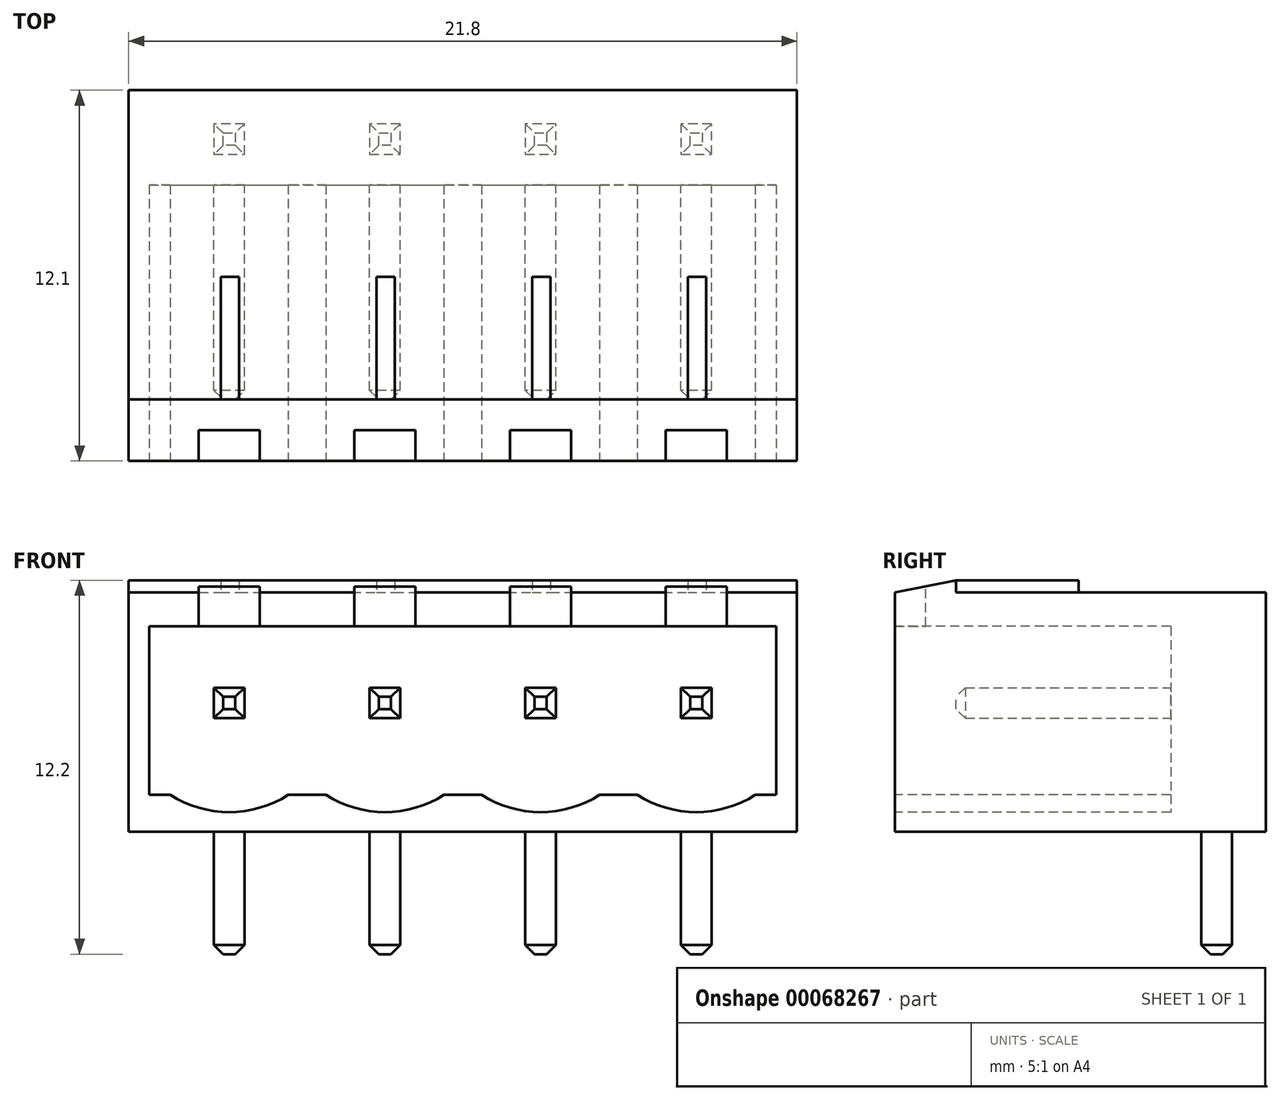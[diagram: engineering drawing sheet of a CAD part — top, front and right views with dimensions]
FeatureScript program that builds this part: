
annotation { "Feature Type Name" : "Feature", "Feature Type Description" : "" }
export const myFeature = defineFeature(function(context is Context, id is Id, definition is map)
    precondition{}
    {
        {
            var Q0;
            Q0=qCreatedBy(makeId("Front.planeOp"),FACE);
            var sketch = newSketch(context, id + "F0", { "sketchPlane" : qUnion([Q0])});
            skLineSegment(sketch, "E0.bottom", {"start": v(-10.9, 4.1) * mm, "end": v(10.9, 4.1) * mm});
            skLineSegment(sketch, "E0.top", {"start": v(-10.9, -4.1) * mm, "end": v(10.9, -4.1) * mm});
            skLineSegment(sketch, "E0.left", {"start": v(-10.9, 4.1) * mm, "end": v(-10.9, -4.1) * mm});
            skLineSegment(sketch, "E0.right", {"start": v(10.9, 4.1) * mm, "end": v(10.9, -4.1) * mm});
            skPoint(sketch, "E0.middle", {"position": v(0, 0) * mm});
            skSolve(sketch);
        }
        {
            var Q0;
            Q0=makeQuery(id+"F0.imprint","IMPRINT",FACE,{"disambiguationData":[TD([[makeQuery(id+"F0.imprint","IMPRINT",EDGE,{"derivedFrom":sQuery(id+"F0.wireOp",EDGE,"E0.bottom")}),-1.0]])]});
            extrude(context, id + "F1", {"entities" : qUnion([Q0]), "endBound" : BoundingType.SYMMETRIC, "depth" : 12.1 * mm});
        }
        {
            var Q0;
            Q0=makeQuery(id+"F1.opExtrude","CAP_FACE",FACE,{"disambiguationData":[OSD([sQuery(id+"F0.wireOp",EDGE,"E0.bottom"),sQuery(id+"F0.wireOp",EDGE,"E0.top"),sQuery(id+"F0.wireOp",EDGE,"E0.left"),sQuery(id+"F0.wireOp",EDGE,"E0.right")])],"isStart":false});
            var sketch = newSketch(context, id + "F2", { "sketchPlane" : qUnion([Q0])});
            skPoint(sketch, "E1.middle", {"position": v(0, 0) * mm});
            skLineSegment(sketch, "E2.bottom", {"start": v(-10.23, 2.6) * mm, "end": v(10.23, 2.6) * mm});
            skLineSegment(sketch, "E2.top", {"start": v(-10.23, -2.4) * mm, "end": v(10.23, -2.4) * mm, "construction": true});
            skLineSegment(sketch, "E2.left", {"start": v(-10.23, 2.6) * mm, "end": v(-10.23, -2.4) * mm});
            skLineSegment(sketch, "E2.right", {"start": v(10.23, 2.6) * mm, "end": v(10.23, -2.4) * mm});
            skPoint(sketch, "E3", {"position": v(-2.54, 0.1) * mm});
            skPoint(sketch, "E4", {"position": v(-7.62, 0.1) * mm});
            skLineSegment(sketch, "E5", {"start": v(-10.23, 0.1) * mm, "end": v(10.23, 0.1) * mm, "construction": true});
            skArc(sketch, "E6", {"start": v(0, -2.4) * mm, "mid": v(-2.54, -3.46) * mm, "end": v(-5.08, -2.4) * mm});
            skArc(sketch, "E7", {"start": v(-5.08, -2.4) * mm, "mid": v(-7.62, -3.46) * mm, "end": v(-10.16, -2.4) * mm});
            skLineSegment(sketch, "E8", {"start": v(0, 12.68) * mm, "end": v(0, -9.6) * mm, "construction": true});
            skPoint(sketch, "E9", {"position": v(2.54, 0.1) * mm});
            skPoint(sketch, "E10", {"position": v(7.62, 0.1) * mm});
            skPoint(sketch, "E11", {"position": v(0, 9.54) * mm});
            skArc(sketch, "E12", {"start": v(0, -2.4) * mm, "mid": v(2.54, -3.46) * mm, "end": v(5.08, -2.4) * mm});
            skArc(sketch, "E13", {"start": v(5.08, -2.4) * mm, "mid": v(7.62, -3.46) * mm, "end": v(10.16, -2.4) * mm});
            skLineSegment(sketch, "E14", {"start": v(10.23, -2.4) * mm, "end": v(10.16, -2.4) * mm});
            skLineSegment(sketch, "E15", {"start": v(-10.16, -2.4) * mm, "end": v(-10.23, -2.4) * mm});
            skSolve(sketch);
        }
        {
            var Q0;
            Q0=qSketchRegion(id+"F2",true);
            extrude(context, id + "F3", {"entities" : qUnion([Q0]), "operationType" : NewBodyOperationType.REMOVE, "oppositeDirection" : true, "depth" : 9 * mm});
        }
        {
            var Q0;
            Q0=makeQuery(id+"F3.boolean.opBoolean","COPY",FACE,{"derivedFrom":makeQuery(id+"F3.opExtrude","CAP_FACE",FACE,{"disambiguationData":[OSD([sQuery(id+"F2.wireOp",EDGE,"E2.bottom"),sQuery(id+"F2.wireOp",EDGE,"E2.left"),sQuery(id+"F2.wireOp",EDGE,"E2.right"),sQuery(id+"F2.wireOp",EDGE,"E6"),sQuery(id+"F2.wireOp",EDGE,"E7"),sQuery(id+"F2.wireOp",EDGE,"E12"),sQuery(id+"F2.wireOp",EDGE,"E13"),sQuery(id+"F2.wireOp",EDGE,"E14"),sQuery(id+"F2.wireOp",EDGE,"E15")])],"isStart":false})});
            var sketch = newSketch(context, id + "F4", { "sketchPlane" : qUnion([Q0])});
            skLineSegment(sketch, "E16.bottom", {"start": v(-7.12, -0.4) * mm, "end": v(-8.12, -0.4) * mm});
            skLineSegment(sketch, "E16.top", {"start": v(-7.12, 0.6) * mm, "end": v(-8.12, 0.6) * mm});
            skLineSegment(sketch, "E16.left", {"start": v(-7.12, -0.4) * mm, "end": v(-7.12, 0.6) * mm});
            skLineSegment(sketch, "E16.right", {"start": v(-8.12, -0.4) * mm, "end": v(-8.12, 0.6) * mm});
            skPoint(sketch, "E16.middle", {"position": v(-7.62, 0.1) * mm});
            skLineSegment(sketch, "E17.bottom", {"start": v(-2.04, -0.4) * mm, "end": v(-3.04, -0.4) * mm});
            skLineSegment(sketch, "E17.top", {"start": v(-2.04, 0.6) * mm, "end": v(-3.04, 0.6) * mm});
            skLineSegment(sketch, "E17.left", {"start": v(-2.04, -0.4) * mm, "end": v(-2.04, 0.6) * mm});
            skLineSegment(sketch, "E17.right", {"start": v(-3.04, -0.4) * mm, "end": v(-3.04, 0.6) * mm});
            skPoint(sketch, "E17.middle", {"position": v(-2.54, 0.1) * mm});
            skLineSegment(sketch, "E18.bottom", {"start": v(3.04, -0.4) * mm, "end": v(2.04, -0.4) * mm});
            skLineSegment(sketch, "E18.top", {"start": v(3.04, 0.6) * mm, "end": v(2.04, 0.6) * mm});
            skLineSegment(sketch, "E18.left", {"start": v(3.04, -0.4) * mm, "end": v(3.04, 0.6) * mm});
            skLineSegment(sketch, "E18.right", {"start": v(2.04, -0.4) * mm, "end": v(2.04, 0.6) * mm});
            skPoint(sketch, "E18.middle", {"position": v(2.54, 0.1) * mm});
            skLineSegment(sketch, "E19.bottom", {"start": v(8.12, -0.4) * mm, "end": v(7.12, -0.4) * mm});
            skLineSegment(sketch, "E19.top", {"start": v(8.12, 0.6) * mm, "end": v(7.12, 0.6) * mm});
            skLineSegment(sketch, "E19.left", {"start": v(8.12, -0.4) * mm, "end": v(8.12, 0.6) * mm});
            skLineSegment(sketch, "E19.right", {"start": v(7.12, -0.4) * mm, "end": v(7.12, 0.6) * mm});
            skPoint(sketch, "E19.middle", {"position": v(7.62, 0.1) * mm});
            skLineSegment(sketch, "E20", {"start": v(10.9, 0.1) * mm, "end": v(-10.9, 0.1) * mm, "construction": true});
            skPoint(sketch, "E20.startSnap0", {"position": v(10.23, 0.1) * mm});
            skPoint(sketch, "E20.endSnap0", {"position": v(-10.23, 0.1) * mm});
            skLineSegment(sketch, "E21", {"start": v(0, 4.1) * mm, "end": v(0, -4.1) * mm, "construction": true});
            skPoint(sketch, "E21.startSnap0", {"position": v(0, 2.6) * mm});
            skSolve(sketch);
        }
        {
            var Q0;
            Q0=qSketchRegion(id+"F4",true);
            var Q1;
            Q1=makeQuery(id+"F1.opExtrude","CAP_FACE",FACE,{"disambiguationData":[OSD([sQuery(id+"F0.wireOp",EDGE,"E0.bottom"),sQuery(id+"F0.wireOp",EDGE,"E0.top"),sQuery(id+"F0.wireOp",EDGE,"E0.left"),sQuery(id+"F0.wireOp",EDGE,"E0.right")])],"isStart":false});
            extrude(context, id + "F5", {"entities" : qUnion([Q0]), "endBoundEntityFace" : qUnion([Q1]), "depth" : 7 * mm});
        }
        {
            var Q0;
            Q0=makeQuery(id+"F1.opExtrude","SWEPT_FACE",FACE,{"disambiguationData":[OSD([sQuery(id+"F0.wireOp",EDGE,"E0.top")])]});
            var sketch = newSketch(context, id + "F6", { "sketchPlane" : qUnion([Q0])});
            skLineSegment(sketch, "E22", {"start": v(0, 6.05) * mm, "end": v(0, -6.05) * mm, "construction": true});
            skLineSegment(sketch, "E23.bottom", {"start": v(-8.12, -3.95) * mm, "end": v(-7.12, -3.95) * mm});
            skLineSegment(sketch, "E23.top", {"start": v(-8.12, -4.95) * mm, "end": v(-7.12, -4.95) * mm});
            skLineSegment(sketch, "E23.left", {"start": v(-8.12, -3.95) * mm, "end": v(-8.12, -4.95) * mm});
            skLineSegment(sketch, "E23.right", {"start": v(-7.12, -3.95) * mm, "end": v(-7.12, -4.95) * mm});
            skPoint(sketch, "E23.middle", {"position": v(-7.62, -4.45) * mm});
            skLineSegment(sketch, "E24.bottom", {"start": v(-3.04, -3.95) * mm, "end": v(-2.04, -3.95) * mm});
            skLineSegment(sketch, "E24.top", {"start": v(-3.04, -4.95) * mm, "end": v(-2.04, -4.95) * mm});
            skLineSegment(sketch, "E24.left", {"start": v(-3.04, -3.95) * mm, "end": v(-3.04, -4.95) * mm});
            skLineSegment(sketch, "E24.right", {"start": v(-2.04, -3.95) * mm, "end": v(-2.04, -4.95) * mm});
            skPoint(sketch, "E24.middle", {"position": v(-2.54, -4.45) * mm});
            skLineSegment(sketch, "E25", {"start": v(-10.9, -4.45) * mm, "end": v(10.9, -4.45) * mm, "construction": true});
            skPoint(sketch, "E25.startSnap0", {"position": v(-8.12, -4.45) * mm});
            skLineSegment(sketch, "E26.MirrorCS", {"start": v(8.12, -3.95) * mm, "end": v(8.12, -4.95) * mm});
            skLineSegment(sketch, "E27.MirrorCS", {"start": v(7.12, -3.95) * mm, "end": v(7.12, -4.95) * mm});
            skLineSegment(sketch, "E28.MirrorCS", {"start": v(3.04, -3.95) * mm, "end": v(2.04, -3.95) * mm});
            skLineSegment(sketch, "E29.MirrorCS", {"start": v(3.04, -4.95) * mm, "end": v(2.04, -4.95) * mm});
            skLineSegment(sketch, "E30.MirrorCS", {"start": v(8.12, -4.95) * mm, "end": v(7.12, -4.95) * mm});
            skPoint(sketch, "E31.MirrorP", {"position": v(2.54, -4.45) * mm});
            skLineSegment(sketch, "E32.MirrorCS", {"start": v(3.04, -3.95) * mm, "end": v(3.04, -4.95) * mm});
            skLineSegment(sketch, "E33.MirrorCS", {"start": v(2.04, -3.95) * mm, "end": v(2.04, -4.95) * mm});
            skPoint(sketch, "E34.MirrorP", {"position": v(8.12, -4.45) * mm});
            skPoint(sketch, "E35.MirrorP", {"position": v(7.62, -4.45) * mm});
            skLineSegment(sketch, "E36.MirrorCS", {"start": v(8.12, -3.95) * mm, "end": v(7.12, -3.95) * mm});
            skSolve(sketch);
        }
        {
            var Q0;
            Q0=qSketchRegion(id+"F6",true);
            extrude(context, id + "F7", {"entities" : qUnion([Q0]), "depth" : 4 * mm});
        }
        {
            var Q0;
            Q0=makeQuery(id+"F1.opExtrude","SWEPT_FACE",FACE,{"disambiguationData":[OSD([sQuery(id+"F0.wireOp",EDGE,"E0.bottom")])]});
            var sketch = newSketch(context, id + "F8", { "sketchPlane" : qUnion([Q0])});
            skLineSegment(sketch, "E37", {"start": v(0, 6.05) * mm, "end": v(0, -6.05) * mm, "construction": true});
            skLineSegment(sketch, "E38.bottom", {"start": v(-3.54, -5.05) * mm, "end": v(-1.54, -5.05) * mm});
            skLineSegment(sketch, "E38.top", {"start": v(-3.54, -6.05) * mm, "end": v(-1.54, -6.05) * mm});
            skLineSegment(sketch, "E38.left", {"start": v(-3.54, -5.05) * mm, "end": v(-3.54, -6.05) * mm});
            skLineSegment(sketch, "E38.right", {"start": v(-1.54, -5.05) * mm, "end": v(-1.54, -6.05) * mm});
            skPoint(sketch, "E38.middle", {"position": v(-2.54, -5.55) * mm});
            skLineSegment(sketch, "E39.1.0.0", {"start": v(3.54, -5.05) * mm, "end": v(3.54, -6.05) * mm});
            skLineSegment(sketch, "E39.1.0.1", {"start": v(1.54, -5.05) * mm, "end": v(1.54, -6.05) * mm});
            skLineSegment(sketch, "E39.1.0.2", {"start": v(1.54, -6.05) * mm, "end": v(3.54, -6.05) * mm});
            skLineSegment(sketch, "E39.1.0.3", {"start": v(1.54, -5.05) * mm, "end": v(3.54, -5.05) * mm});
            skPoint(sketch, "E39.1.0.4", {"position": v(2.54, -5.55) * mm});
            skLineSegment(sketch, "E39.2.0.0", {"start": v(8.62, -5.05) * mm, "end": v(8.62, -6.05) * mm});
            skLineSegment(sketch, "E39.2.0.1", {"start": v(6.62, -5.05) * mm, "end": v(6.62, -6.05) * mm});
            skLineSegment(sketch, "E39.2.0.2", {"start": v(6.62, -6.05) * mm, "end": v(8.62, -6.05) * mm});
            skLineSegment(sketch, "E39.2.0.3", {"start": v(6.62, -5.05) * mm, "end": v(8.62, -5.05) * mm});
            skPoint(sketch, "E39.2.0.4", {"position": v(7.62, -5.55) * mm});
            skLineSegment(sketch, "E39.direction1", {"start": v(-1.54, -6.05) * mm, "end": v(3.54, -6.05) * mm, "construction": true});
            skLineSegment(sketch, "E40.1.0.0", {"start": v(-8.62, -5.05) * mm, "end": v(-6.62, -5.05) * mm});
            skLineSegment(sketch, "E40.1.0.1", {"start": v(-8.62, -6.05) * mm, "end": v(-6.62, -6.05) * mm});
            skLineSegment(sketch, "E40.1.0.2", {"start": v(-8.62, -5.05) * mm, "end": v(-8.62, -6.05) * mm});
            skLineSegment(sketch, "E40.1.0.3", {"start": v(-6.62, -5.05) * mm, "end": v(-6.62, -6.05) * mm});
            skPoint(sketch, "E40.1.0.4", {"position": v(-7.62, -5.55) * mm});
            skLineSegment(sketch, "E40.direction1", {"start": v(-3.54, -5.05) * mm, "end": v(-8.62, -5.05) * mm, "construction": true});
            skSolve(sketch);
        }
        {
            var Q0;
            Q0=qSketchRegion(id+"F8",true);
            extrude(context, id + "F9", {"entities" : qUnion([Q0]), "operationType" : NewBodyOperationType.REMOVE, "oppositeDirection" : true, "depth" : 2 * mm});
        }
        {
            var Q0;
            {var subQ0=sQuery(id+"F0.wireOp",EDGE,"E0.top");var subQ1=sQuery(id+"F0.wireOp",EDGE,"E0.bottom");var subQ2=sQuery(id+"F0.wireOp",EDGE,"E0.left");var subQ3=sQuery(id+"F0.wireOp",EDGE,"E0.right");Q0=makeQuery(id+"F9.boolean.opBoolean","SPLIT",FACE,{"disambiguationData":[TD([makeQuery(id+"F1.opExtrude","SWEPT_FACE",FACE,{"disambiguationData":[OSD([subQ0])]})])],"derivedFrom":makeQuery(id+"F1.opExtrude","CAP_FACE",FACE,{"disambiguationData":[OSD([subQ1,subQ0,subQ2,subQ3])],"isStart":false})});}
            var sketch = newSketch(context, id + "F10", { "sketchPlane" : qUnion([Q0])});
            skLineSegment(sketch, "E41.bottom", {"start": v(-10.23, -2.4) * mm, "end": v(10.23, -2.4) * mm});
            skLineSegment(sketch, "E41.top", {"start": v(-10.23, -2.9) * mm, "end": v(10.23, -2.9) * mm});
            skLineSegment(sketch, "E41.left", {"start": v(-10.23, -2.4) * mm, "end": v(-10.23, -2.9) * mm});
            skLineSegment(sketch, "E41.right", {"start": v(10.23, -2.4) * mm, "end": v(10.23, -2.9) * mm});
            skSolve(sketch);
        }
        {
            var Q0;
            Q0=qSketchRegion(id+"F10",true);
            var Q1;
            Q1=makeQuery(id+"F3.boolean.opBoolean","COPY",FACE,{"derivedFrom":makeQuery(id+"F3.opExtrude","CAP_FACE",FACE,{"disambiguationData":[OSD([sQuery(id+"F2.wireOp",EDGE,"E2.bottom"),sQuery(id+"F2.wireOp",EDGE,"E2.left"),sQuery(id+"F2.wireOp",EDGE,"E2.right"),sQuery(id+"F2.wireOp",EDGE,"E6"),sQuery(id+"F2.wireOp",EDGE,"E7"),sQuery(id+"F2.wireOp",EDGE,"E12"),sQuery(id+"F2.wireOp",EDGE,"E13"),sQuery(id+"F2.wireOp",EDGE,"E14"),sQuery(id+"F2.wireOp",EDGE,"E15")])],"isStart":false})});
            extrude(context, id + "F11", {"entities" : qUnion([Q0]), "operationType" : NewBodyOperationType.REMOVE, "endBound" : BoundingType.UP_TO_SURFACE, "oppositeDirection" : true, "endBoundEntityFace" : qUnion([Q1]), "depth" : 25 * mm});
        }
        {
            var Q0;
            Q0=makeQuery(id+"F5.opExtrude","CAP_FACE",FACE,{"disambiguationData":[OSD([sQuery(id+"F4.wireOp",EDGE,"E16.bottom"),sQuery(id+"F4.wireOp",EDGE,"E16.top"),sQuery(id+"F4.wireOp",EDGE,"E16.left"),sQuery(id+"F4.wireOp",EDGE,"E16.right")])],"isStart":false});
            var Q1;
            Q1=makeQuery(id+"F5.opExtrude","CAP_FACE",FACE,{"disambiguationData":[OSD([sQuery(id+"F4.wireOp",EDGE,"E17.bottom"),sQuery(id+"F4.wireOp",EDGE,"E17.top"),sQuery(id+"F4.wireOp",EDGE,"E17.left"),sQuery(id+"F4.wireOp",EDGE,"E17.right")])],"isStart":false});
            var Q2;
            Q2=makeQuery(id+"F5.opExtrude","CAP_FACE",FACE,{"disambiguationData":[OSD([sQuery(id+"F4.wireOp",EDGE,"E18.bottom"),sQuery(id+"F4.wireOp",EDGE,"E18.top"),sQuery(id+"F4.wireOp",EDGE,"E18.left"),sQuery(id+"F4.wireOp",EDGE,"E18.right")])],"isStart":false});
            var Q3;
            Q3=makeQuery(id+"F5.opExtrude","CAP_FACE",FACE,{"disambiguationData":[OSD([sQuery(id+"F4.wireOp",EDGE,"E19.bottom"),sQuery(id+"F4.wireOp",EDGE,"E19.top"),sQuery(id+"F4.wireOp",EDGE,"E19.left"),sQuery(id+"F4.wireOp",EDGE,"E19.right")])],"isStart":false});
            var Q4;
            Q4=makeQuery(id+"F7.opExtrude","CAP_FACE",FACE,{"disambiguationData":[OSD([sQuery(id+"F6.wireOp",EDGE,"E23.bottom"),sQuery(id+"F6.wireOp",EDGE,"E23.top"),sQuery(id+"F6.wireOp",EDGE,"E23.left"),sQuery(id+"F6.wireOp",EDGE,"E23.right")])],"isStart":false});
            var Q5;
            Q5=makeQuery(id+"F7.opExtrude","CAP_FACE",FACE,{"disambiguationData":[OSD([sQuery(id+"F6.wireOp",EDGE,"E24.bottom"),sQuery(id+"F6.wireOp",EDGE,"E24.top"),sQuery(id+"F6.wireOp",EDGE,"E24.left"),sQuery(id+"F6.wireOp",EDGE,"E24.right")])],"isStart":false});
            var Q6;
            Q6=makeQuery(id+"F7.opExtrude","CAP_FACE",FACE,{"disambiguationData":[OSD([sQuery(id+"F6.wireOp",EDGE,"E28.MirrorCS"),sQuery(id+"F6.wireOp",EDGE,"E29.MirrorCS"),sQuery(id+"F6.wireOp",EDGE,"E32.MirrorCS"),sQuery(id+"F6.wireOp",EDGE,"E33.MirrorCS")])],"isStart":false});
            var Q7;
            Q7=makeQuery(id+"F7.opExtrude","CAP_FACE",FACE,{"disambiguationData":[OSD([sQuery(id+"F6.wireOp",EDGE,"E26.MirrorCS"),sQuery(id+"F6.wireOp",EDGE,"E27.MirrorCS"),sQuery(id+"F6.wireOp",EDGE,"E30.MirrorCS"),sQuery(id+"F6.wireOp",EDGE,"E36.MirrorCS")])],"isStart":false});
            chamfer(context, id + "F12", {"entities" : qUnion([Q0, Q1, Q2, Q3, Q4, Q5, Q6, Q7]), "width" : 0.3 * mm, "tangentPropagation" : true});
        }
        {
            var Q0;
            Q0=makeQuery(id+"F1.opExtrude","SWEPT_FACE",FACE,{"disambiguationData":[OSD([sQuery(id+"F0.wireOp",EDGE,"E0.right")])]});
            var sketch = newSketch(context, id + "F13", { "sketchPlane" : qUnion([Q0])});
            skLineSegment(sketch, "E42", {"start": v(-6.05, 4.1) * mm, "end": v(-6.05, 3.7) * mm});
            skLineSegment(sketch, "E43", {"start": v(-6.05, 3.7) * mm, "end": v(-4.05, 4.1) * mm});
            skLineSegment(sketch, "E44", {"start": v(-4.05, 4.1) * mm, "end": v(-6.05, 4.1) * mm});
            skLineSegment(sketch, "E45", {"start": v(-4.05, 4.1) * mm, "end": v(-4.05, 3.7) * mm});
            skLineSegment(sketch, "E46", {"start": v(-4.05, 3.7) * mm, "end": v(6.05, 3.7) * mm});
            skLineSegment(sketch, "E47", {"start": v(6.05, 3.7) * mm, "end": v(6.05, 4.1) * mm});
            skLineSegment(sketch, "E48", {"start": v(6.05, 4.1) * mm, "end": v(-4.05, 4.1) * mm});
            skSolve(sketch);
        }
        {
            var Q0;
            Q0=qSketchRegion(id+"F13",true);
            extrude(context, id + "F14", {"entities" : qUnion([Q0]), "operationType" : NewBodyOperationType.REMOVE, "endBound" : BoundingType.THROUGH_ALL, "oppositeDirection" : true, "depth" : 25 * mm});
        }
        {
            var Q0;
            Q0=makeQuery(id+"F14.boolean.opBoolean","COPY",FACE,{"derivedFrom":makeQuery(id+"F14.opExtrude","SWEPT_FACE",FACE,{"disambiguationData":[OSD([sQuery(id+"F13.wireOp",EDGE,"E46")])]})});
            var sketch = newSketch(context, id + "F15", { "sketchPlane" : qUnion([Q0])});
            skLineSegment(sketch, "E49.bottom", {"start": v(-7.9, -4.05) * mm, "end": v(-7.3, -4.05) * mm});
            skLineSegment(sketch, "E49.top", {"start": v(-7.9, -0.05) * mm, "end": v(-7.3, -0.05) * mm});
            skLineSegment(sketch, "E49.left", {"start": v(-7.9, -4.05) * mm, "end": v(-7.9, -0.05) * mm});
            skLineSegment(sketch, "E49.right", {"start": v(-7.3, -4.05) * mm, "end": v(-7.3, -0.05) * mm});
            skLineSegment(sketch, "E50.1.0.0", {"start": v(-2.82, -4.05) * mm, "end": v(-2.22, -4.05) * mm});
            skLineSegment(sketch, "E50.1.0.1", {"start": v(-2.82, -0.05) * mm, "end": v(-2.22, -0.05) * mm});
            skLineSegment(sketch, "E50.1.0.2", {"start": v(-2.82, -4.05) * mm, "end": v(-2.82, -0.05) * mm});
            skLineSegment(sketch, "E50.1.0.3", {"start": v(-2.22, -4.05) * mm, "end": v(-2.22, -0.05) * mm});
            skLineSegment(sketch, "E50.2.0.0", {"start": v(2.26, -4.05) * mm, "end": v(2.86, -4.05) * mm});
            skLineSegment(sketch, "E50.2.0.1", {"start": v(2.26, -0.05) * mm, "end": v(2.86, -0.05) * mm});
            skLineSegment(sketch, "E50.2.0.2", {"start": v(2.26, -4.05) * mm, "end": v(2.26, -0.05) * mm});
            skLineSegment(sketch, "E50.2.0.3", {"start": v(2.86, -4.05) * mm, "end": v(2.86, -0.05) * mm});
            skLineSegment(sketch, "E50.3.0.0", {"start": v(7.34, -4.05) * mm, "end": v(7.94, -4.05) * mm});
            skLineSegment(sketch, "E50.3.0.1", {"start": v(7.34, -0.05) * mm, "end": v(7.94, -0.05) * mm});
            skLineSegment(sketch, "E50.3.0.2", {"start": v(7.34, -4.05) * mm, "end": v(7.34, -0.05) * mm});
            skLineSegment(sketch, "E50.3.0.3", {"start": v(7.94, -4.05) * mm, "end": v(7.94, -0.05) * mm});
            skLineSegment(sketch, "E50.direction1", {"start": v(-7.9, -4.05) * mm, "end": v(-2.82, -4.05) * mm, "construction": true});
            skSolve(sketch);
        }
        {
            var Q0;
            Q0=qSketchRegion(id+"F15",true);
            extrude(context, id + "F16", {"entities" : qUnion([Q0]), "operationType" : NewBodyOperationType.ADD, "depth" : 0.4 * mm});
        }
    });
